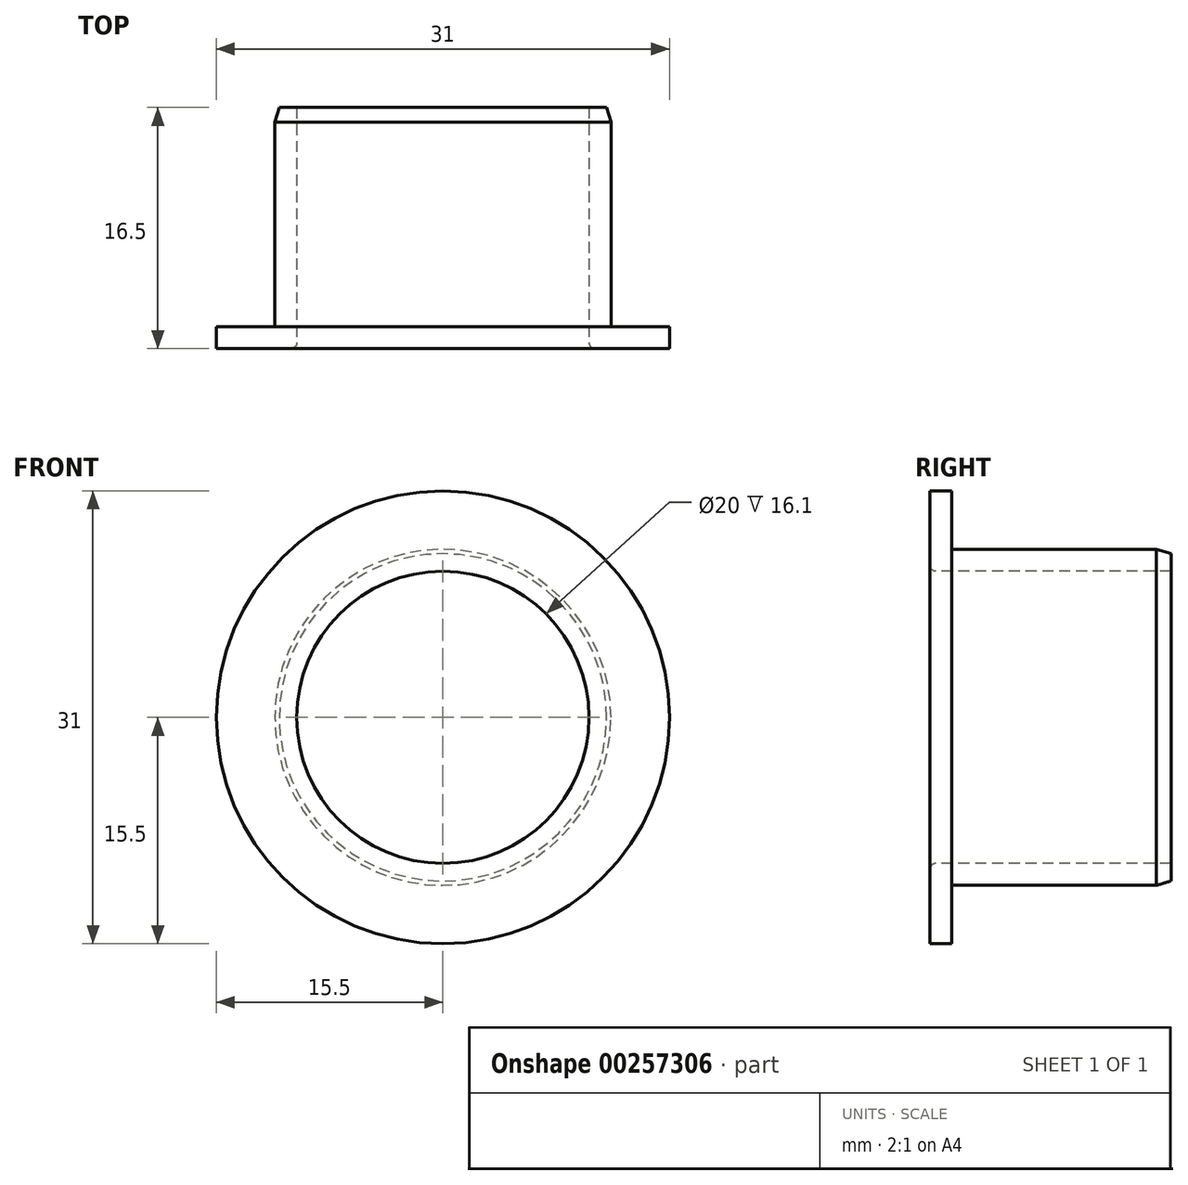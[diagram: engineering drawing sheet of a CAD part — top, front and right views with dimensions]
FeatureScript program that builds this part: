
annotation { "Feature Type Name" : "Feature", "Feature Type Description" : "" }
export const myFeature = defineFeature(function(context is Context, id is Id, definition is map)
    precondition{}
    {
        {
            var Q0;
            Q0=qCreatedBy(makeId("Right.planeOp"),FACE);
            var sketch = newSketch(context, id + "F0", { "sketchPlane" : qUnion([Q0])});
            skLineSegment(sketch, "E0", {"start": v(0, 15.5) * mm, "end": v(0, 10) * mm});
            skLineSegment(sketch, "E1", {"start": v(0, 10) * mm, "end": v(16.5, 10) * mm});
            skLineSegment(sketch, "E2", {"start": v(16.5, 10) * mm, "end": v(16.5, 11.5) * mm});
            skLineSegment(sketch, "E3", {"start": v(16.5, 11.5) * mm, "end": v(1.5, 11.5) * mm});
            skLineSegment(sketch, "E4", {"start": v(1.5, 11.5) * mm, "end": v(1.5, 15.5) * mm});
            skLineSegment(sketch, "E5", {"start": v(1.5, 15.5) * mm, "end": v(0, 15.5) * mm});
            skLineSegment(sketch, "E6", {"start": v(-13.86, 0) * mm, "end": v(32.97, 0) * mm, "construction": true});
            skSolve(sketch);
        }
        {
            var Q0;
            Q0=makeQuery(id+"F0.imprint","IMPRINT",FACE,{"disambiguationData":[TD([[makeQuery(id+"F0.imprint","IMPRINT",EDGE,{"derivedFrom":sQuery(id+"F0.wireOp",EDGE,"E0")}),1.0]])]});
            var Q1;
            Q1=sQuery(id+"F0.wireOp",EDGE,"E6");
            revolve(context, id + "F1", {"entities" : qUnion([Q0]), "axis" : qUnion([Q1]), "revolveType" : RevolveType.FULL});
        }
        {
            var Q0;
            Q0=makeQuery(id+"F1.opRevolve","SWEPT_EDGE",EDGE,{"disambiguationData":[OSD([sQuery(id+"F0.wireOp",EDGE,"E0"),sQuery(id+"F0.wireOp",EDGE,"E1")])]});
            fillet(context, id + "F2", {"entities" : qUnion([Q0]), "radius" : 0.4 * mm, "tangentPropagation" : true, "allowEdgeOverflow" : false});
        }
        {
            var Q0;
            Q0=makeQuery(id+"F1.opRevolve","SWEPT_EDGE",EDGE,{"disambiguationData":[OSD([sQuery(id+"F0.wireOp",EDGE,"E2"),sQuery(id+"F0.wireOp",EDGE,"E3")])]});
            chamfer(context, id + "F3", {"entities" : qUnion([Q0]), "chamferType" : ChamferType.TWO_OFFSETS, "width1" : 1 * mm, "oppositeDirection" : false, "width2" : 0.3 * mm, "tangentPropagation" : true});
        }
    });
